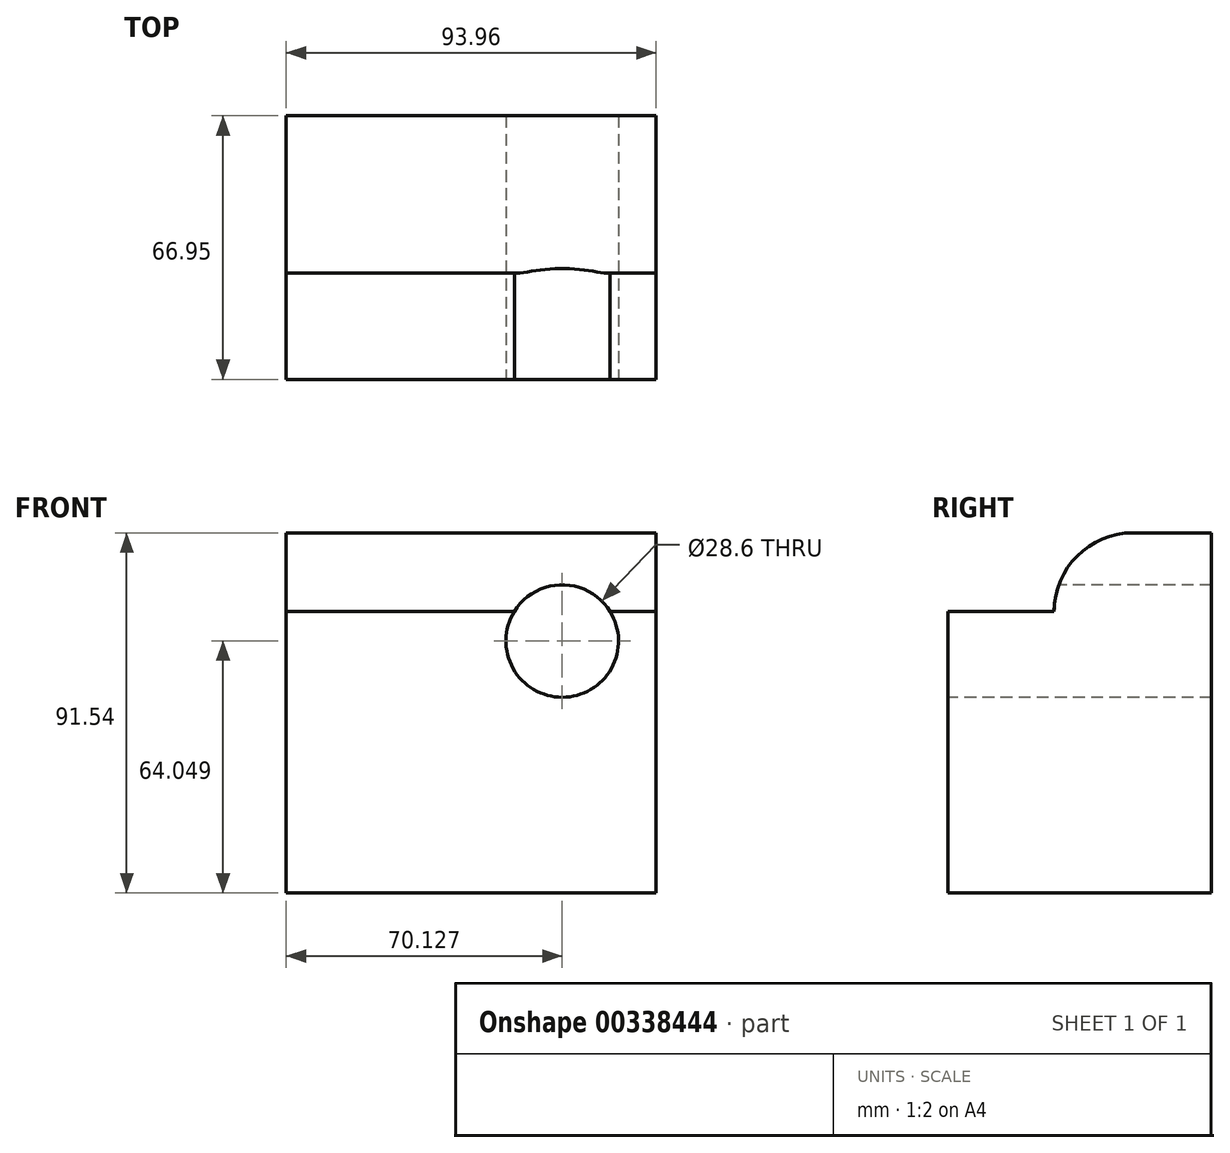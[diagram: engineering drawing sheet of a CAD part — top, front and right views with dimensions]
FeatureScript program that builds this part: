
annotation { "Feature Type Name" : "Feature", "Feature Type Description" : "" }
export const myFeature = defineFeature(function(context is Context, id is Id, definition is map)
    precondition{}
    {
        {
            var Q0;
            Q0=qCreatedBy(makeId("Front.planeOp"),FACE);
            var sketch = newSketch(context, id + "F0", { "sketchPlane" : qUnion([Q0])});
            skLineSegment(sketch, "E0.bottom", {"start": v(46.98, 45.77) * mm, "end": v(-46.98, 45.77) * mm});
            skLineSegment(sketch, "E0.top", {"start": v(46.98, -45.77) * mm, "end": v(-46.98, -45.77) * mm});
            skLineSegment(sketch, "E0.left", {"start": v(46.98, 45.77) * mm, "end": v(46.98, -45.77) * mm});
            skLineSegment(sketch, "E0.right", {"start": v(-46.98, 45.77) * mm, "end": v(-46.98, -45.77) * mm});
            skPoint(sketch, "E0.middle", {"position": v(0, 0) * mm});
            skSolve(sketch);
        }
        {
            var Q0;
            Q0 = qSketchRegion(id + "F0", true);
            extrude(context, id + "F1", {"entities" : qUnion([Q0]), "depth" : 40 * mm});
        }
        {
            var Q0;
            Q0=makeQuery(id+"F1.opExtrude","CAP_FACE",FACE,{"disambiguationData":[OSD([sQuery(id+"F0.wireOp",EDGE,"E0.bottom"),sQuery(id+"F0.wireOp",EDGE,"E0.top"),sQuery(id+"F0.wireOp",EDGE,"E0.left"),sQuery(id+"F0.wireOp",EDGE,"E0.right")])],"isStart":false});
            var sketch = newSketch(context, id + "F2", { "sketchPlane" : qUnion([Q0])});
            skCircle(sketch, "E1", {"center": v(23.15, 18.28) * mm, "radius": 14.3 * mm});
            skSolve(sketch);
        }
        {
            var Q0;
            Q0 = qSketchRegion(id + "F2", true);
            extrude(context, id + "F3", {"entities" : qUnion([Q0]), "operationType" : NewBodyOperationType.REMOVE, "oppositeDirection" : true, "depth" : 64.57 * mm});
        }
        {
            var Q0;
            Q0=makeQuery(id+"F1.opExtrude","CAP_EDGE",EDGE,{"disambiguationData":[OSD([sQuery(id+"F0.wireOp",EDGE,"E0.bottom")])],"isStart":false});
            fillet(context, id + "F4", {"entities" : qUnion([Q0]), "radius" : 20 * mm, "tangentPropagation" : true, "allowEdgeOverflow" : false});
        }
        {
            var Q0;
            Q0=makeQuery(id+"F1.opExtrude","CAP_FACE",FACE,{"disambiguationData":[OSD([sQuery(id+"F0.wireOp",EDGE,"E0.bottom"),sQuery(id+"F0.wireOp",EDGE,"E0.top"),sQuery(id+"F0.wireOp",EDGE,"E0.left"),sQuery(id+"F0.wireOp",EDGE,"E0.right")])],"isStart":false});
            var sketch = newSketch(context, id + "F5", { "sketchPlane" : qUnion([Q0])});
            skSolve(sketch);
        }
        {
            var Q0;
            {var subQ2=sQuery(id+"F0.wireOp",EDGE,"E0.top");Q0=makeQuery(id+"F5.imprint","IMPRINT",FACE,{"disambiguationData":[TD([[makeQuery(id+"F5.imprint","IMPRINT",EDGE,{"derivedFrom":makeQuery(id+"F1.opExtrude","CAP_EDGE",EDGE,{"disambiguationData":[OSD([subQ2])],"isStart":false})}),-1.0]])]});}
            extrude(context, id + "F6", {"entities" : qUnion([Q0]), "operationType" : NewBodyOperationType.ADD, "depth" : 26.95 * mm});
        }
    });
